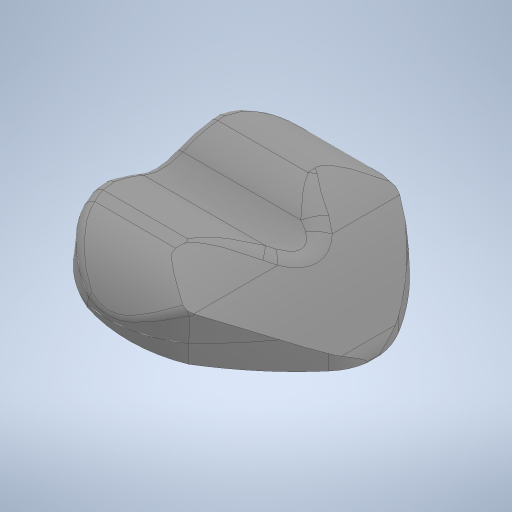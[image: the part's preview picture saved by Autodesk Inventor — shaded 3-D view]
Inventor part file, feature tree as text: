
AUTODESK INVENTOR PART (.ipt)
format: ipt  version: 2024 (Build 280153000, 153)  size: 795,648 bytes
history: native  units: mm
features: other x3, plane x2, extrude x2, sketch x2
ambient origin geometry x8: Origin, YZ Plane, XZ Plane, XY Plane, X Axis, Y Axis, Z Axis, Center Point
bodies: Body1 (feature_tree)
feature tree (9):
  other  "Tubo.ipt"
  plane  "Plano de trabajo1"
  extrude  "Extrusión1"  Depth=38.0mm
  plane  "Plano de trabajo2"
  extrude  "Extrusión2"  Depth=10.0mm
  other  "Sólido2::Tubo.ipt"
  other  "OperaciónIdentificador1"
  sketch  "Boceto1"  dims[d0=25.0mm d1=38.0mm]
  sketch  "Boceto2"  dims[d2=100.0mm d3=0.0mm d4=21.5mm d5=20.0mm d6=15.0mm d7=10.0mm d8=0.0mm]
